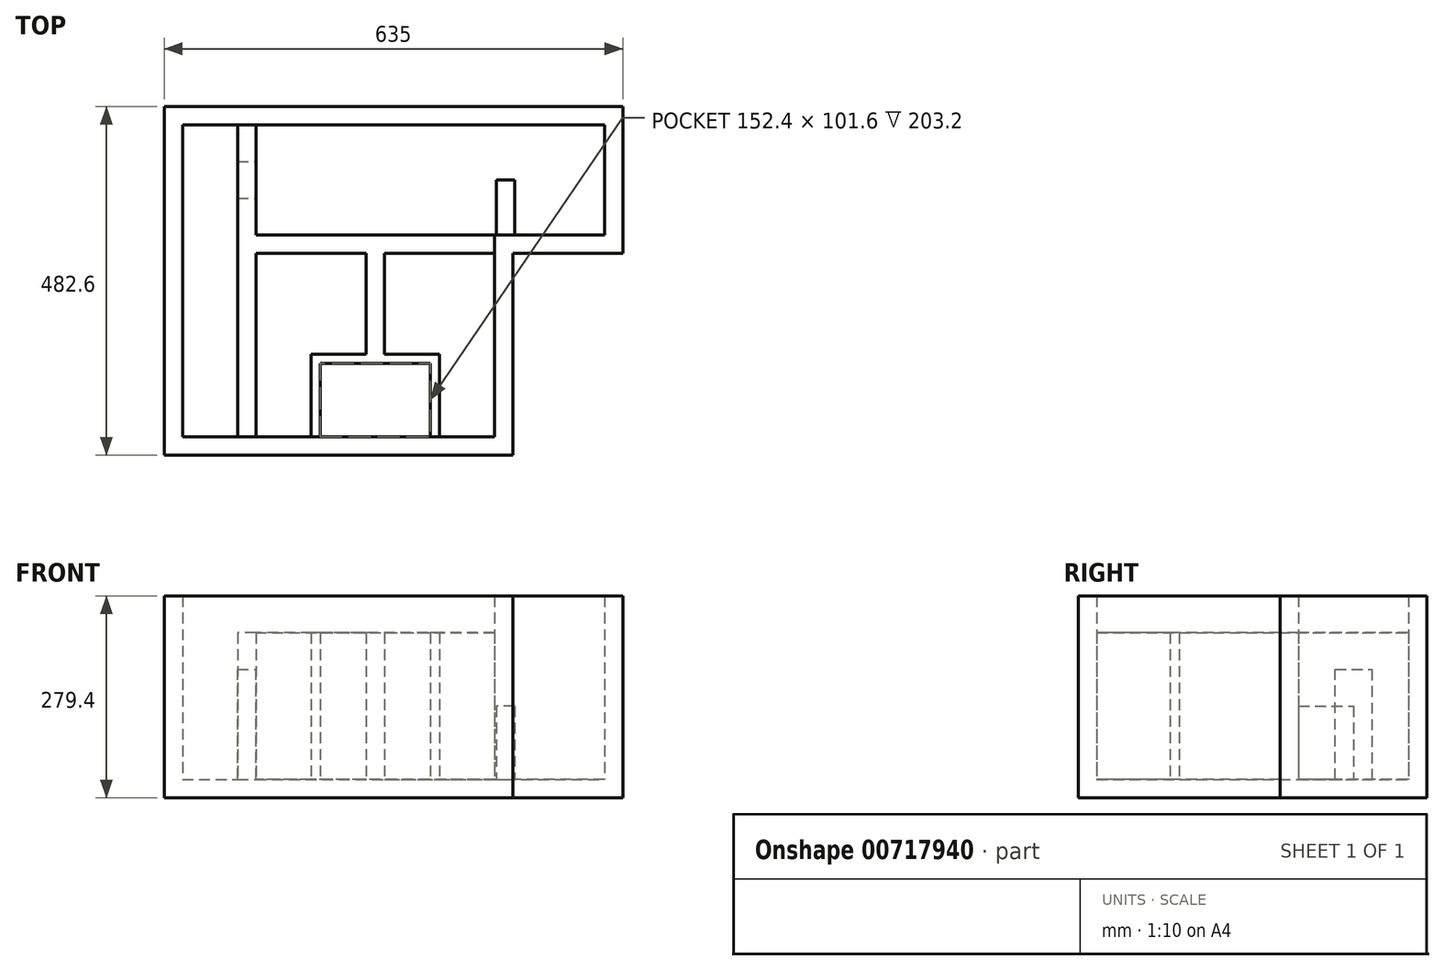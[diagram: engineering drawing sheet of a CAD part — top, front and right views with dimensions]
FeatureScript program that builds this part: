
annotation { "Feature Type Name" : "Feature", "Feature Type Description" : "" }
export const myFeature = defineFeature(function(context is Context, id is Id, definition is map)
    precondition{}
    {
        {
            var Q0;
            Q0=qCreatedBy(makeId("Top.planeOp"),FACE);
            var sketch = newSketch(context, id + "F0", { "sketchPlane" : qUnion([Q0])});
            skLineSegment(sketch, "E0", {"start": v(0, 0) * mm, "end": v(0, 279.4) * mm});
            skLineSegment(sketch, "E1", {"start": v(0, 279.4) * mm, "end": v(152.4, 279.4) * mm});
            skLineSegment(sketch, "E2", {"start": v(152.4, 279.4) * mm, "end": v(152.4, 482.6) * mm});
            skLineSegment(sketch, "E3", {"start": v(152.4, 482.6) * mm, "end": v(-482.6, 482.6) * mm});
            skLineSegment(sketch, "E4", {"start": v(-482.6, 482.6) * mm, "end": v(-482.6, 0) * mm});
            skLineSegment(sketch, "E5", {"start": v(-482.6, 0) * mm, "end": v(0, 0) * mm});
            skSolve(sketch);
        }
        {
            var Q0;
            Q0 = qSketchRegion(id + "F0", true);
            extrude(context, id + "F1", {"entities" : qUnion([Q0]), "depth" : 25.4 * mm, "offsetDistance" : 25.4 * mm});
        }
        {
            var Q0;
            Q0=makeQuery(id+"F1.opExtrude","CAP_FACE",FACE,{"disambiguationData":[OSD([sQuery(id+"F0.wireOp",EDGE,"E0"),sQuery(id+"F0.wireOp",EDGE,"E1"),sQuery(id+"F0.wireOp",EDGE,"E2"),sQuery(id+"F0.wireOp",EDGE,"E3"),sQuery(id+"F0.wireOp",EDGE,"E4"),sQuery(id+"F0.wireOp",EDGE,"E5")])],"isStart":false});
            var sketch = newSketch(context, id + "F2", { "sketchPlane" : qUnion([Q0])});
            skLineSegment(sketch, "E6", {"start": v(-457.2, 25.4) * mm, "end": v(-457.2, 457.2) * mm});
            skLineSegment(sketch, "E7", {"start": v(-457.2, 457.2) * mm, "end": v(127, 457.2) * mm});
            skLineSegment(sketch, "E8", {"start": v(127, 457.2) * mm, "end": v(127, 304.8) * mm});
            skLineSegment(sketch, "E9", {"start": v(127, 304.8) * mm, "end": v(-25.4, 304.8) * mm});
            skLineSegment(sketch, "E10", {"start": v(-25.4, 304.8) * mm, "end": v(-25.4, 25.4) * mm});
            skLineSegment(sketch, "E11", {"start": v(-25.4, 25.4) * mm, "end": v(-457.2, 25.4) * mm});
            skLineSegment(sketch, "E12.0", {"start": v(152.4, 482.6) * mm, "end": v(-482.6, 482.6) * mm});
            skLineSegment(sketch, "E12.1", {"start": v(152.4, 279.4) * mm, "end": v(152.4, 482.6) * mm});
            skLineSegment(sketch, "E12.2", {"start": v(0, 279.4) * mm, "end": v(152.4, 279.4) * mm});
            skLineSegment(sketch, "E12.3", {"start": v(0, 0) * mm, "end": v(0, 279.4) * mm});
            skLineSegment(sketch, "E12.4", {"start": v(-482.6, 0) * mm, "end": v(0, 0) * mm});
            skLineSegment(sketch, "E12.5", {"start": v(-482.6, 482.6) * mm, "end": v(-482.6, 0) * mm});
            skSolve(sketch);
        }
        {
            var Q0;
            Q0 = qSketchRegion(id + "F2", true);
            extrude(context, id + "F3", {"entities" : qUnion([Q0]), "operationType" : NewBodyOperationType.ADD, "depth" : 254 * mm, "offsetDistance" : 25.4 * mm});
        }
        {
            var Q0;
            Q0=makeQuery(id+"F1.opExtrude","CAP_FACE",FACE,{"disambiguationData":[OSD([sQuery(id+"F0.wireOp",EDGE,"E0"),sQuery(id+"F0.wireOp",EDGE,"E1"),sQuery(id+"F0.wireOp",EDGE,"E2"),sQuery(id+"F0.wireOp",EDGE,"E3"),sQuery(id+"F0.wireOp",EDGE,"E4"),sQuery(id+"F0.wireOp",EDGE,"E5")])],"isStart":false});
            var sketch = newSketch(context, id + "F4", { "sketchPlane" : qUnion([Q0])});
            skLineSegment(sketch, "E13", {"start": v(-381, 25.4) * mm, "end": v(-381, 457.2) * mm});
            skLineSegment(sketch, "E14", {"start": v(-25.4, 304.8) * mm, "end": v(-381, 304.8) * mm});
            skLineSegment(sketch, "E15", {"start": v(-355.6, 457.2) * mm, "end": v(-355.6, 25.4) * mm});
            skLineSegment(sketch, "E16", {"start": v(-381, 279.4) * mm, "end": v(-25.4, 279.4) * mm});
            skLineSegment(sketch, "E17", {"start": v(-203.2, 279.4) * mm, "end": v(-203.2, 25.4) * mm});
            skLineSegment(sketch, "E18", {"start": v(-177.8, 279.4) * mm, "end": v(-177.8, 25.4) * mm});
            skLineSegment(sketch, "E19", {"start": v(-203.2, 127) * mm, "end": v(-279.4, 127) * mm});
            skLineSegment(sketch, "E20", {"start": v(-279.4, 127) * mm, "end": v(-279.4, 25.4) * mm});
            skLineSegment(sketch, "E21", {"start": v(-177.8, 127) * mm, "end": v(-101.6, 127) * mm});
            skLineSegment(sketch, "E22", {"start": v(-101.6, 127) * mm, "end": v(-101.6, 25.4) * mm});
            skLineSegment(sketch, "E23", {"start": v(-203.2, 127) * mm, "end": v(-177.8, 127) * mm});
            skLineSegment(sketch, "E24", {"start": v(-203.2, 139.7) * mm, "end": v(-279.4, 139.7) * mm});
            skLineSegment(sketch, "E25", {"start": v(-279.4, 139.7) * mm, "end": v(-279.4, 127) * mm});
            skLineSegment(sketch, "E26", {"start": v(-203.2, 139.7) * mm, "end": v(-101.6, 139.7) * mm});
            skLineSegment(sketch, "E27", {"start": v(-101.6, 139.7) * mm, "end": v(-101.6, 127) * mm});
            skLineSegment(sketch, "E28", {"start": v(-114.3, 139.7) * mm, "end": v(-114.3, 25.4) * mm});
            skLineSegment(sketch, "E29", {"start": v(-266.7, 139.7) * mm, "end": v(-266.7, 25.4) * mm});
            skSolve(sketch);
        }
        {
            var Q0;
            Q0 = qSketchRegion(id + "F4", true);
            var Q1;
            {var subQ0=sQuery(id+"F4.wireOp",EDGE,"E13");var subQ1=makeQuery(id+"F3.opExtrude","CAP_EDGE",EDGE,{"disambiguationData":[OSD([sQuery(id+"F2.wireOp",EDGE,"E11")])],"isStart":true});var subQ2=makeQuery(id+"F4.imprint","INTERSECT",VERTEX,{"derivedFrom":[subQ1,subQ0]});Q1=makeQuery(id+"F4.imprint","IMPRINT",FACE,{"disambiguationData":[TD([[makeQuery(id+"F4.imprint","IMPRINT",EDGE,{"disambiguationData":[TD([[subQ2,-1.0]])],"derivedFrom":subQ0}),-1.0]])]});}
            var Q2;
            {var subQ3=sQuery(id+"F4.wireOp",EDGE,"E15");var subQ5=sQuery(id+"F4.wireOp",EDGE,"E14");var subQ9=makeQuery(id+"F4.imprint","INTERSECT",VERTEX,{"derivedFrom":[subQ5,subQ3]});Q2=makeQuery(id+"F4.imprint","IMPRINT",FACE,{"disambiguationData":[TD([[makeQuery(id+"F4.imprint","IMPRINT",EDGE,{"disambiguationData":[TD([[subQ9,-1.0]])],"derivedFrom":subQ3}),1.0]])]});}
            var Q3;
            {var subQ0=sQuery(id+"F4.wireOp",EDGE,"E13");var subQ1=makeQuery(id+"F3.opExtrude","CAP_EDGE",EDGE,{"disambiguationData":[OSD([sQuery(id+"F2.wireOp",EDGE,"E7")])],"isStart":true});var subQ2=makeQuery(id+"F4.imprint","INTERSECT",VERTEX,{"derivedFrom":[subQ1,subQ0]});Q3=makeQuery(id+"F4.imprint","IMPRINT",FACE,{"disambiguationData":[TD([[makeQuery(id+"F4.imprint","IMPRINT",EDGE,{"disambiguationData":[TD([[subQ2,1.0]])],"derivedFrom":subQ0}),-1.0]])]});}
            var Q4;
            {var subQ0=sQuery(id+"F4.wireOp",EDGE,"E22");Q4=makeQuery(id+"F4.imprint","IMPRINT",FACE,{"disambiguationData":[TD([[makeQuery(id+"F4.imprint","IMPRINT",EDGE,{"derivedFrom":subQ0}),-1.0]])]});}
            var Q5;
            {var subQ0=sQuery(id+"F4.wireOp",EDGE,"E20");Q5=makeQuery(id+"F4.imprint","IMPRINT",FACE,{"disambiguationData":[TD([[makeQuery(id+"F4.imprint","IMPRINT",EDGE,{"derivedFrom":subQ0}),1.0]])]});}
            extrude(context, id + "F5", {"entities" : qUnion([Q0, Q1, Q2, Q3, Q4, Q5]), "operationType" : NewBodyOperationType.ADD, "depth" : 203.2 * mm, "offsetDistance" : 25.4 * mm});
        }
        {
            var Q0;
            Q0=makeQuery(id+"F5.boolean.opBoolean","SPLIT",FACE,{"disambiguationData":[TD([makeQuery(id+"F3.opExtrude","SWEPT_FACE",FACE,{"disambiguationData":[OSD([sQuery(id+"F2.wireOp",EDGE,"E8")])]})])],"derivedFrom":makeQuery(id+"F1.opExtrude","CAP_FACE",FACE,{"disambiguationData":[OSD([sQuery(id+"F0.wireOp",EDGE,"E0"),sQuery(id+"F0.wireOp",EDGE,"E1"),sQuery(id+"F0.wireOp",EDGE,"E2"),sQuery(id+"F0.wireOp",EDGE,"E3"),sQuery(id+"F0.wireOp",EDGE,"E4"),sQuery(id+"F0.wireOp",EDGE,"E5")])],"isStart":false})});
            var sketch = newSketch(context, id + "F6", { "sketchPlane" : qUnion([Q0])});
            skLineSegment(sketch, "E30", {"start": v(-22.62, 304.8) * mm, "end": v(-22.62, 381) * mm});
            skLineSegment(sketch, "E31", {"start": v(-22.62, 381) * mm, "end": v(2.78, 381) * mm});
            skLineSegment(sketch, "E32", {"start": v(2.78, 381) * mm, "end": v(2.78, 304.8) * mm});
            skLineSegment(sketch, "E33", {"start": v(2.78, 304.8) * mm, "end": v(-22.62, 304.8) * mm});
            skSolve(sketch);
        }
        {
            var Q0;
            Q0 = qSketchRegion(id + "F6", true);
            extrude(context, id + "F7", {"entities" : qUnion([Q0]), "operationType" : NewBodyOperationType.ADD, "depth" : 101.6 * mm, "offsetDistance" : 25.4 * mm});
        }
        {
            var Q0;
            {var subQ0=sQuery(id+"F4.wireOp",EDGE,"E15");Q0=makeQuery(id+"F5.opExtrude","SWEPT_FACE",FACE,{"disambiguationData":[OSD([subQ0]),TDD([makeQuery(id+"F4.imprint","IMPRINT",EDGE,{"disambiguationData":[TD([[makeQuery(id+"F4.imprint","INTERSECT",VERTEX,{"derivedFrom":[makeQuery(id+"F3.opExtrude","CAP_EDGE",EDGE,{"disambiguationData":[OSD([sQuery(id+"F2.wireOp",EDGE,"E7")])],"isStart":true}),subQ0]}),-1.0]])],"derivedFrom":subQ0})])]});}
            var sketch = newSketch(context, id + "F8", { "sketchPlane" : qUnion([Q0])});
            skLineSegment(sketch, "E34", {"start": v(355.6, 25.4) * mm, "end": v(355.6, 177.8) * mm});
            skLineSegment(sketch, "E35", {"start": v(406.4, 25.4) * mm, "end": v(355.6, 25.4) * mm});
            skLineSegment(sketch, "E36", {"start": v(355.6, 177.8) * mm, "end": v(406.4, 177.8) * mm});
            skLineSegment(sketch, "E37", {"start": v(406.4, 177.8) * mm, "end": v(406.4, 25.4) * mm});
            skSolve(sketch);
        }
        {
            var Q0;
            Q0 = qSketchRegion(id + "F8", true);
            extrude(context, id + "F9", {"entities" : qUnion([Q0]), "operationType" : NewBodyOperationType.REMOVE, "oppositeDirection" : true, "depth" : 25.4 * mm, "offsetDistance" : 25.4 * mm});
        }
    });
